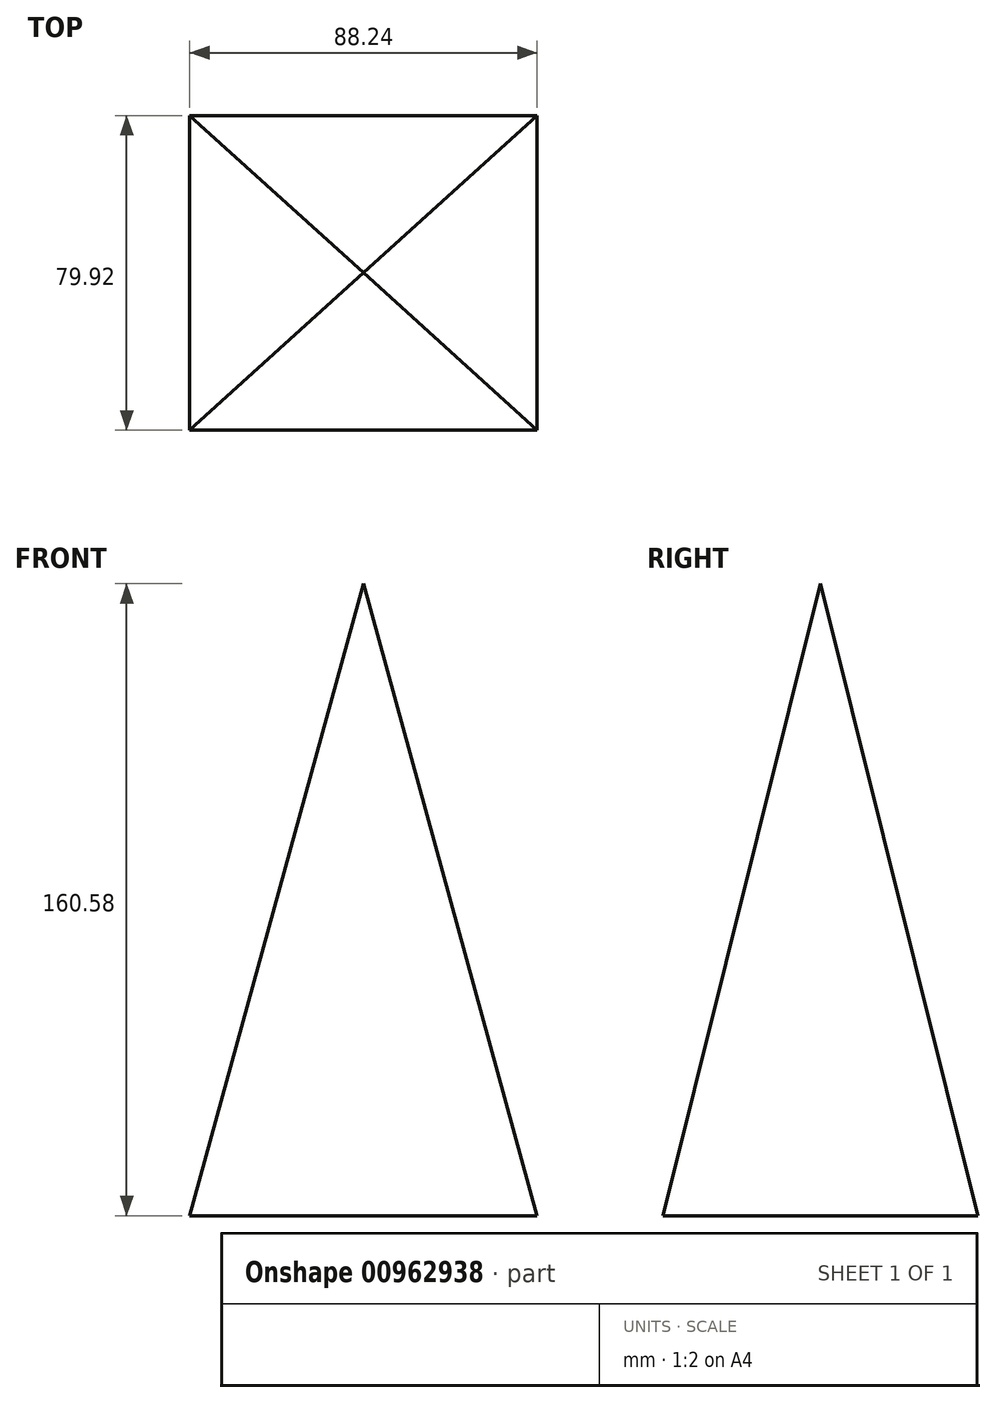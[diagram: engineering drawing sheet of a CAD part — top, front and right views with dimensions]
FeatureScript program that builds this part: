
annotation { "Feature Type Name" : "Feature", "Feature Type Description" : "" }
export const myFeature = defineFeature(function(context is Context, id is Id, definition is map)
    precondition{}
    {
        {
            var Q0;
            Q0=qCreatedBy(makeId("Top.planeOp"),FACE);
            var sketch = newSketch(context, id + "F0", { "sketchPlane" : qUnion([Q0])});
            skLineSegment(sketch, "E0.bottom", {"start": v(44.12, -39.96) * mm, "end": v(-44.12, -39.96) * mm});
            skLineSegment(sketch, "E0.top", {"start": v(44.12, 39.96) * mm, "end": v(-44.12, 39.96) * mm});
            skLineSegment(sketch, "E0.left", {"start": v(44.12, -39.96) * mm, "end": v(44.12, 39.96) * mm});
            skLineSegment(sketch, "E0.right", {"start": v(-44.12, -39.96) * mm, "end": v(-44.12, 39.96) * mm});
            skPoint(sketch, "E0.middle", {"position": v(0, 0) * mm});
            skSolve(sketch);
        }
        {
            var Q0;
            Q0=qCreatedBy(makeId("Front.planeOp"),FACE);
            var sketch = newSketch(context, id + "F1", { "sketchPlane" : qUnion([Q0])});
            skPoint(sketch, "E1", {"position": v(0, 160.58) * mm});
            skSolve(sketch);
        }
        {
            var Q0;
            Q0 = qSketchRegion(id + "F0", true);
            var Q1;
            Q1=sQuery(id+"F1.wireOp",VERTEX,"E1");
            loft(context, id + "F2", {"sheetProfilesArray" : [{ "sheetProfileEntities" : qUnion([Q0]) }, { "sheetProfileEntities" : qUnion([Q1]) }]});
        }
    });
